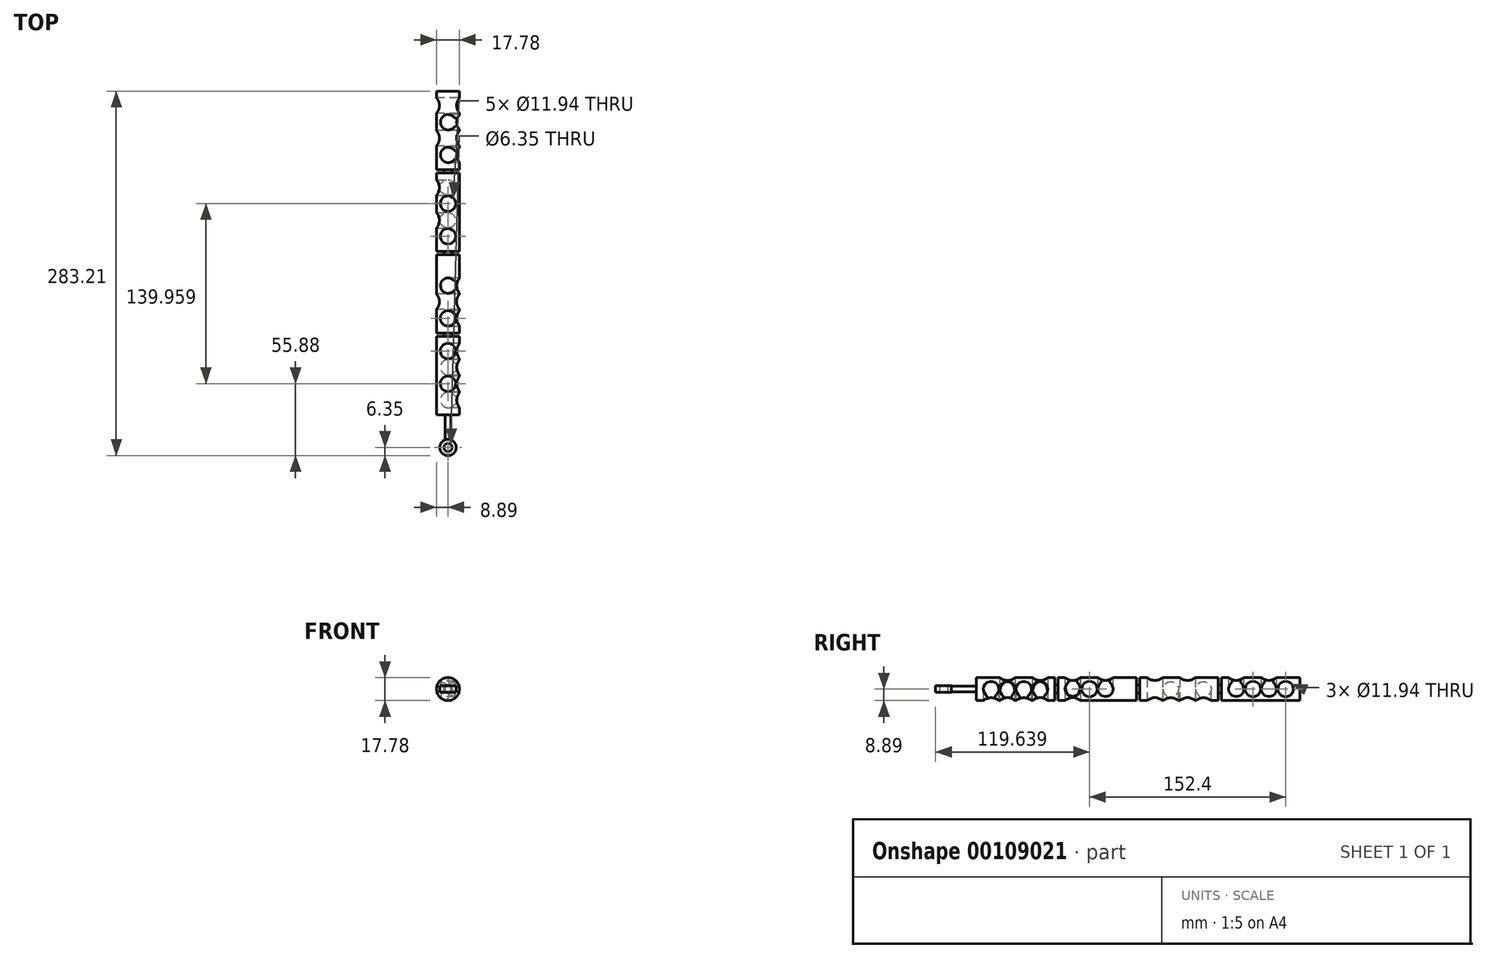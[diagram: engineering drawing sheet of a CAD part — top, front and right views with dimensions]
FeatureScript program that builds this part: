
annotation { "Feature Type Name" : "Feature", "Feature Type Description" : "" }
export const myFeature = defineFeature(function(context is Context, id is Id, definition is map)
    precondition{}
    {
        {
            var Q0;
            Q0=qCreatedBy(makeId("Front.planeOp"),FACE);
            var sketch = newSketch(context, id + "F0", { "sketchPlane" : qUnion([Q0])});
            skCircle(sketch, "E0", {"center": v(0, 0) * mm, "radius": 8.9 * mm});
            skSolve(sketch);
        }
        {
            var Q0;
            Q0=makeQuery(id+"F0.imprint","IMPRINT",FACE,{"disambiguationData":[TD([[makeQuery(id+"F0.imprint","IMPRINT",EDGE,{"derivedFrom":sQuery(id+"F0.wireOp",EDGE,"E0")}),1.0]])]});
            extrude(context, id + "F1", {"entities" : qUnion([Q0]), "oppositeDirection" : true, "depth" : 50.8 * mm});
        }
        {
            var Q0;
            Q0=qCreatedBy(makeId("Top.planeOp"),FACE);
            var sketch = newSketch(context, id + "F2", { "sketchPlane" : qUnion([Q0])});
            skCircle(sketch, "E1", {"center": v(0, 6.6) * mm, "radius": 5.97 * mm});
            skCircle(sketch, "E2", {"center": v(0, 32) * mm, "radius": 5.97 * mm});
            skLineSegment(sketch, "E3", {"start": v(0, 32) * mm, "end": v(0, 6.6) * mm});
            skLineSegment(sketch, "E4", {"start": v(0, 26.04) * mm, "end": v(0, 12.58) * mm});
            skSolve(sketch);
        }
        {
            var Q0;
            Q0=qCreatedBy(makeId("Top.planeOp"),FACE);
            cPlane(context, id + "F3", {"entities" : qUnion([Q0]), "cplaneType" : CPlaneType.OFFSET, "offset" : 25.4 * mm, "oppositeDirection" : true, "width" : 152.4 * mm, "height" : 152.4 * mm});
        }
        {
            var Q0;
            Q0=qCreatedBy(id+"F3.planeOp",FACE);
            var sketch = newSketch(context, id + "F4", { "sketchPlane" : qUnion([Q0])});
            skCircle(sketch, "E5", {"center": v(0, 19.05) * mm, "radius": 5.97 * mm});
            skLineSegment(sketch, "E6", {"start": v(0, 19.05) * mm, "end": v(0, 0) * mm});
            skLineSegment(sketch, "E7", {"start": v(0, 19.05) * mm, "end": v(0, 44.45) * mm});
            skCircle(sketch, "E8", {"center": v(0, 44.45) * mm, "radius": 5.97 * mm});
            skSolve(sketch);
        }
        {
            var Q0;
            Q0=qCreatedBy(makeId("Front.planeOp"),FACE);
            var sketch = newSketch(context, id + "F5", { "sketchPlane" : qUnion([Q0])});
            skLineSegment(sketch, "E9", {"start": v(0, -25.4) * mm, "end": v(0, -8.9) * mm});
            skArc(sketch, "E10", {"start": v(0, -8.89) * mm, "mid": v(2.6, -2.6) * mm, "end": v(8.9, 0) * mm});
            skLineSegment(sketch, "E11", {"start": v(8.9, 0) * mm, "end": v(29, 0) * mm});
            skLineSegment(sketch, "E12", {"start": v(-8.9, 0) * mm, "end": v(-22.24, 0) * mm});
            skArc(sketch, "E13", {"start": v(-8.9, 0) * mm, "mid": v(-2.6, -2.6) * mm, "end": v(0, -8.9) * mm});
            skSolve(sketch);
        }
        {
            var Q0;
            Q0=makeQuery(id+"F2.imprint","IMPRINT",FACE,{"disambiguationData":[TD([[makeQuery(id+"F2.imprint","IMPRINT",EDGE,{"derivedFrom":sQuery(id+"F2.wireOp",EDGE,"E2")}),1.0]])]});
            var Q1;
            Q1=makeQuery(id+"F2.imprint","IMPRINT",FACE,{"disambiguationData":[TD([[makeQuery(id+"F2.imprint","IMPRINT",EDGE,{"derivedFrom":sQuery(id+"F2.wireOp",EDGE,"E1")}),1.0]])]});
            extrude(context, id + "F6", {"entities" : qUnion([Q0, Q1]), "operationType" : NewBodyOperationType.REMOVE, "depth" : 25.4 * mm, "hasSecondDirection" : true, "secondDirectionOppositeDirection" : true, "secondDirectionDepth" : 25.4 * mm});
        }
        {
            var Q0;
            Q0=makeQuery(id+"F1.opExtrude","CAP_FACE",FACE,{"disambiguationData":[OSD([sQuery(id+"F0.wireOp",EDGE,"E0")])],"isStart":true});
            var sketch = newSketch(context, id + "F7", { "sketchPlane" : qUnion([Q0])});
            skCircle(sketch, "E14", {"center": v(0, 0) * mm, "radius": 3.18 * mm});
            skSolve(sketch);
        }
        {
            var Q0;
            Q0=makeQuery(id+"F7.imprint","IMPRINT",FACE,{"disambiguationData":[TD([[makeQuery(id+"F7.imprint","IMPRINT",EDGE,{"derivedFrom":sQuery(id+"F7.wireOp",EDGE,"E14")}),1.0]])]});
            extrude(context, id + "F8", {"entities" : qUnion([Q0]), "operationType" : NewBodyOperationType.ADD, "depth" : 12.7 * mm});
        }
        {
            var Q0;
            Q0=makeQuery(id+"F1.opExtrude","CAP_FACE",FACE,{"disambiguationData":[OSD([sQuery(id+"F0.wireOp",EDGE,"E0")])],"isStart":false});
            var sketch = newSketch(context, id + "F9", { "sketchPlane" : qUnion([Q0])});
            skCircle(sketch, "E15", {"center": v(0, 0) * mm, "radius": 3.18 * mm});
            skSolve(sketch);
        }
        {
            var Q0;
            Q0 = qSketchRegion(id + "F9", true);
            extrude(context, id + "F10", {"entities" : qUnion([Q0]), "operationType" : NewBodyOperationType.ADD, "depth" : 12.7 * mm});
        }
        {
            var Q0;
            Q0=makeQuery(id+"F8.opExtrude","CAP_FACE",FACE,{"disambiguationData":[OSD([sQuery(id+"F7.wireOp",EDGE,"E14")])],"isStart":false});
            var sketch = newSketch(context, id + "F11", { "sketchPlane" : qUnion([Q0])});
            skCircle(sketch, "E16", {"center": v(0, 0) * mm, "radius": 8.9 * mm});
            skSolve(sketch);
        }
        {
            var Q0;
            Q0=makeQuery(id+"F11.imprint","IMPRINT",FACE,{"disambiguationData":[TD([[makeQuery(id+"F11.imprint","IMPRINT",EDGE,{"derivedFrom":sQuery(id+"F11.wireOp",EDGE,"E16")}),1.0]])]});
            var Q1;
            Q1=makeQuery(id+"F11.imprint","IMPRINT",FACE,{"disambiguationData":[TD([[makeQuery(id+"F11.imprint","IMPRINT",EDGE,{"derivedFrom":makeQuery(id+"F8.opExtrude","CAP_EDGE",EDGE,{"disambiguationData":[OSD([sQuery(id+"F7.wireOp",EDGE,"E14")])],"isStart":false})}),1.0]])]});
            extrude(context, id + "F12", {"entities" : qUnion([Q0, Q1]), "operationType" : NewBodyOperationType.ADD, "depth" : 50.8 * mm});
        }
        {
            var Q0;
            Q0=makeQuery(id+"F10.opExtrude","CAP_FACE",FACE,{"disambiguationData":[OSD([sQuery(id+"F9.wireOp",EDGE,"E15")])],"isStart":false});
            var sketch = newSketch(context, id + "F13", { "sketchPlane" : qUnion([Q0])});
            skCircle(sketch, "E17", {"center": v(0, 0) * mm, "radius": 8.9 * mm});
            skSolve(sketch);
        }
        {
            var Q0;
            Q0=makeQuery(id+"F13.imprint","IMPRINT",FACE,{"disambiguationData":[TD([[makeQuery(id+"F13.imprint","IMPRINT",EDGE,{"derivedFrom":sQuery(id+"F13.wireOp",EDGE,"E17")}),1.0]])]});
            var Q1;
            Q1=makeQuery(id+"F13.imprint","IMPRINT",FACE,{"disambiguationData":[TD([[makeQuery(id+"F13.imprint","IMPRINT",EDGE,{"derivedFrom":makeQuery(id+"F10.opExtrude","CAP_EDGE",EDGE,{"disambiguationData":[OSD([sQuery(id+"F9.wireOp",EDGE,"E15")])],"isStart":false})}),1.0]])]});
            extrude(context, id + "F14", {"entities" : qUnion([Q0, Q1]), "operationType" : NewBodyOperationType.ADD, "depth" : 50.8 * mm});
        }
        {
            var Q0;
            Q0=makeQuery(id+"F12.opExtrude","CAP_FACE",FACE,{"disambiguationData":[OSD([sQuery(id+"F11.wireOp",EDGE,"E16")])],"isStart":false});
            var sketch = newSketch(context, id + "F15", { "sketchPlane" : qUnion([Q0])});
            skCircle(sketch, "E18", {"center": v(0, 0) * mm, "radius": 3.18 * mm});
            skSolve(sketch);
        }
        {
            var Q0;
            Q0=makeQuery(id+"F15.imprint","IMPRINT",FACE,{"disambiguationData":[TD([[makeQuery(id+"F15.imprint","IMPRINT",EDGE,{"derivedFrom":sQuery(id+"F15.wireOp",EDGE,"E18")}),1.0]])]});
            extrude(context, id + "F16", {"entities" : qUnion([Q0]), "operationType" : NewBodyOperationType.ADD, "depth" : 12.7 * mm});
        }
        {
            var Q0;
            Q0=makeQuery(id+"F16.opExtrude","CAP_FACE",FACE,{"disambiguationData":[OSD([sQuery(id+"F15.wireOp",EDGE,"E18")])],"isStart":false});
            var sketch = newSketch(context, id + "F17", { "sketchPlane" : qUnion([Q0])});
            skCircle(sketch, "E19", {"center": v(0, 0) * mm, "radius": 8.9 * mm});
            skSolve(sketch);
        }
        {
            var Q0;
            Q0=makeQuery(id+"F17.imprint","IMPRINT",FACE,{"disambiguationData":[TD([[makeQuery(id+"F17.imprint","IMPRINT",EDGE,{"derivedFrom":makeQuery(id+"F16.opExtrude","CAP_EDGE",EDGE,{"disambiguationData":[OSD([sQuery(id+"F15.wireOp",EDGE,"E18")])],"isStart":false})}),1.0]])]});
            var Q1;
            Q1=makeQuery(id+"F17.imprint","IMPRINT",FACE,{"disambiguationData":[TD([[makeQuery(id+"F17.imprint","IMPRINT",EDGE,{"derivedFrom":sQuery(id+"F17.wireOp",EDGE,"E19")}),1.0]])]});
            extrude(context, id + "F18", {"entities" : qUnion([Q0, Q1]), "operationType" : NewBodyOperationType.ADD, "depth" : 50.8 * mm});
        }
        {
            var Q0;
            Q0=qCreatedBy(makeId("Top.planeOp"),FACE);
            var sketch = newSketch(context, id + "F19", { "sketchPlane" : qUnion([Q0])});
            skLineSegment(sketch, "E20", {"start": v(0, 6.6) * mm, "end": v(0, -18.8) * mm});
            skCircle(sketch, "E21", {"center": v(0, -18.8) * mm, "radius": 5.97 * mm});
            skLineSegment(sketch, "E22", {"start": v(0, -18.8) * mm, "end": v(0, -44.2) * mm});
            skCircle(sketch, "E23", {"center": v(0, -44.2) * mm, "radius": 5.97 * mm});
            skLineSegment(sketch, "E24", {"start": v(0, -44.2) * mm, "end": v(0, -82.3) * mm});
            skCircle(sketch, "E25", {"center": v(0, -82.3) * mm, "radius": 5.97 * mm});
            skLineSegment(sketch, "E26", {"start": v(0, -82.3) * mm, "end": v(0, -107.7) * mm});
            skCircle(sketch, "E27", {"center": v(0, -107.7) * mm, "radius": 5.97 * mm});
            skLineSegment(sketch, "E28", {"start": v(0, 6.6) * mm, "end": v(0, 32) * mm});
            skLineSegment(sketch, "E29", {"start": v(0, 32) * mm, "end": v(0, 82.8) * mm});
            skCircle(sketch, "E30", {"center": v(0, 82.8) * mm, "radius": 6 * mm});
            skLineSegment(sketch, "E31", {"start": v(0, 82.8) * mm, "end": v(0, 108.2) * mm});
            skCircle(sketch, "E32", {"center": v(0, 108.2) * mm, "radius": 5.97 * mm});
            skSolve(sketch);
        }
        {
            var Q0;
            Q0=qCreatedBy(id+"F3.planeOp",FACE);
            var sketch = newSketch(context, id + "F20", { "sketchPlane" : qUnion([Q0])});
            skLineSegment(sketch, "E33", {"start": v(0, 19.05) * mm, "end": v(0, -31.75) * mm});
            skLineSegment(sketch, "E34", {"start": v(0, 44.45) * mm, "end": v(0, 69.85) * mm});
            skLineSegment(sketch, "E35", {"start": v(0, -31.75) * mm, "end": v(0, -57.15) * mm});
            skLineSegment(sketch, "E36", {"start": v(0, -57.15) * mm, "end": v(0, -82.55) * mm});
            skLineSegment(sketch, "E37", {"start": v(0, -82.55) * mm, "end": v(0, -107.95) * mm});
            skLineSegment(sketch, "E38", {"start": v(0, 69.85) * mm, "end": v(0, 95.25) * mm});
            skCircle(sketch, "E39", {"center": v(0, 69.85) * mm, "radius": 5.97 * mm});
            skCircle(sketch, "E40", {"center": v(0, 95.25) * mm, "radius": 5.97 * mm});
            skCircle(sketch, "E41", {"center": v(0, -31.75) * mm, "radius": 5.97 * mm});
            skCircle(sketch, "E42", {"center": v(0, -57.15) * mm, "radius": 5.97 * mm});
            skCircle(sketch, "E43", {"center": v(0, -82.55) * mm, "radius": 5.97 * mm});
            skCircle(sketch, "E44", {"center": v(0, -107.95) * mm, "radius": 5.97 * mm});
            skLineSegment(sketch, "E45", {"start": v(0, -82.55) * mm, "end": v(0, -95.25) * mm});
            skCircle(sketch, "E46", {"center": v(0, -95.25) * mm, "radius": 5.97 * mm});
            skLineSegment(sketch, "E47", {"start": v(0, -107.95) * mm, "end": v(0, -120.65) * mm});
            skCircle(sketch, "E48", {"center": v(0, -120.65) * mm, "radius": 5.97 * mm});
            skLineSegment(sketch, "E49", {"start": v(0, -120.65) * mm, "end": v(0, -127) * mm});
            skSolve(sketch);
        }
        {
            var Q0;
            Q0=qCreatedBy(makeId("Top.planeOp"),FACE);
            cPlane(context, id + "F21", {"entities" : qUnion([Q0]), "cplaneType" : CPlaneType.OFFSET, "offset" : 25.4 * mm, "width" : 152.4 * mm, "height" : 152.4 * mm});
        }
        {
            var Q0;
            Q0=qCreatedBy(makeId("Right.planeOp"),FACE);
            var sketch = newSketch(context, id + "F22", { "sketchPlane" : qUnion([Q0])});
            skLineSegment(sketch, "E50", {"start": v(108.2, 0) * mm, "end": v(82.8, 0) * mm});
            skLineSegment(sketch, "E51", {"start": v(-18.8, 0) * mm, "end": v(-44.2, 0) * mm});
            skLineSegment(sketch, "E52", {"start": v(-44.2, 0) * mm, "end": v(-82.3, 0) * mm});
            skLineSegment(sketch, "E53", {"start": v(-82.3, 0) * mm, "end": v(-107.7, 0) * mm});
            skCircle(sketch, "E54", {"center": v(108.2, 0) * mm, "radius": 5.97 * mm});
            skCircle(sketch, "E55", {"center": v(82.8, 0) * mm, "radius": 5.97 * mm});
            skCircle(sketch, "E56", {"center": v(-18.8, 0) * mm, "radius": 5.97 * mm});
            skCircle(sketch, "E57", {"center": v(-44.2, 0) * mm, "radius": 5.97 * mm});
            skCircle(sketch, "E58", {"center": v(-82.3, 0) * mm, "radius": 5.97 * mm});
            skCircle(sketch, "E59", {"center": v(-107.7, 0) * mm, "radius": 5.97 * mm});
            skLineSegment(sketch, "E60", {"start": v(-44.2, 0) * mm, "end": v(-95, 0) * mm});
            skLineSegment(sketch, "E61", {"start": v(-18.8, 0) * mm, "end": v(82.8, 0) * mm});
            skSolve(sketch);
        }
        {
            var Q0;
            Q0=makeQuery(id+"F22.imprint","IMPRINT",FACE,{"disambiguationData":[TD([[makeQuery(id+"F22.imprint","IMPRINT",EDGE,{"derivedFrom":sQuery(id+"F22.wireOp",EDGE,"E54")}),1.0]])]});
            var Q1;
            {var subQ0=sQuery(id+"F22.wireOp",EDGE,"64IQ4rFp-FNV7-kNIL-IrGJ-L7VyzQQre0IC");var subQ1=sQuery(id+"F22.wireOp",EDGE,"E50");var subQ2=makeQuery(id+"F22.imprint","INTERSECT",VERTEX,{"derivedFrom":[subQ1,subQ0]});Q1=makeQuery(id+"F22.imprint","IMPRINT",FACE,{"disambiguationData":[TD([[makeQuery(id+"F22.imprint","IMPRINT",EDGE,{"disambiguationData":[TD([[subQ2,1.0]])],"derivedFrom":subQ1}),-1.0]])]});}
            var Q2;
            {var subQ0=sQuery(id+"F22.wireOp",EDGE,"64IQ4rFp-FNV7-kNIL-IrGJ-L7VyzQQre0IC");var subQ1=sQuery(id+"F22.wireOp",EDGE,"E50");var subQ2=makeQuery(id+"F22.imprint","INTERSECT",VERTEX,{"derivedFrom":[subQ1,subQ0]});Q2=makeQuery(id+"F22.imprint","IMPRINT",FACE,{"disambiguationData":[TD([[makeQuery(id+"F22.imprint","IMPRINT",EDGE,{"disambiguationData":[TD([[subQ2,1.0]])],"derivedFrom":subQ1}),1.0]])]});}
            var Q3;
            {var subQ0=sQuery(id+"F22.wireOp",EDGE,"E51");var subQ1=sQuery(id+"F22.wireOp",EDGE,"64IQ4rFp-FNV7-kNIL-IrGJ-L7VyzQQre0IC");var subQ2=makeQuery(id+"F22.imprint","INTERSECT",VERTEX,{"derivedFrom":[subQ1,subQ0]});Q3=makeQuery(id+"F22.imprint","IMPRINT",FACE,{"disambiguationData":[TD([[makeQuery(id+"F22.imprint","IMPRINT",EDGE,{"disambiguationData":[TD([[subQ2,1.0]])],"derivedFrom":subQ1}),1.0]])]});}
            var Q4;
            {var subQ0=sQuery(id+"F22.wireOp",EDGE,"E51");var subQ1=sQuery(id+"F22.wireOp",EDGE,"64IQ4rFp-FNV7-kNIL-IrGJ-L7VyzQQre0IC");var subQ2=makeQuery(id+"F22.imprint","INTERSECT",VERTEX,{"derivedFrom":[subQ1,subQ0]});Q4=makeQuery(id+"F22.imprint","IMPRINT",FACE,{"disambiguationData":[TD([[makeQuery(id+"F22.imprint","IMPRINT",EDGE,{"disambiguationData":[TD([[subQ2,1.0]])],"derivedFrom":subQ1}),-1.0]])]});}
            var Q5;
            {var subQ0=sQuery(id+"F22.wireOp",EDGE,"E52");var subQ1=sQuery(id+"F22.wireOp",EDGE,"E51");var subQ2=makeQuery(id+"F22.imprint","INTERSECT",VERTEX,{"derivedFrom":[subQ1,subQ0]});Q5=makeQuery(id+"F22.imprint","IMPRINT",FACE,{"disambiguationData":[TD([[makeQuery(id+"F22.imprint","IMPRINT",EDGE,{"disambiguationData":[TD([[subQ2,1.0]])],"derivedFrom":subQ1}),-1.0]])]});}
            var Q6;
            {var subQ0=sQuery(id+"F22.wireOp",EDGE,"E52");var subQ1=sQuery(id+"F22.wireOp",EDGE,"E51");var subQ2=makeQuery(id+"F22.imprint","INTERSECT",VERTEX,{"derivedFrom":[subQ1,subQ0]});Q6=makeQuery(id+"F22.imprint","IMPRINT",FACE,{"disambiguationData":[TD([[makeQuery(id+"F22.imprint","IMPRINT",EDGE,{"disambiguationData":[TD([[subQ2,1.0]])],"derivedFrom":subQ1}),1.0]])]});}
            var Q7;
            Q7=sQuery(id+"F22.wireOp",EDGE,"E54");
            extrude(context, id + "F23", {"entities" : qUnion([Q0, Q1, Q2, Q3, Q4, Q5, Q6]), "operationType" : NewBodyOperationType.REMOVE, "surfaceEntities" : qUnion([Q7]), "depth" : 25.4 * mm, "hasSecondDirection" : true, "secondDirectionOppositeDirection" : true, "secondDirectionDepth" : 25.4 * mm});
        }
        {
            var Q0;
            Q0=qCreatedBy(id+"F21.planeOp",FACE);
            var sketch = newSketch(context, id + "F24", { "sketchPlane" : qUnion([Q0])});
            skLineSegment(sketch, "E62", {"start": v(0, 69.85) * mm, "end": v(0, 116.23) * mm});
            skCircle(sketch, "E63", {"center": v(0, 69.85) * mm, "radius": 5.97 * mm});
            skCircle(sketch, "E64", {"center": v(0, 95.25) * mm, "radius": 5.97 * mm});
            skCircle(sketch, "E65", {"center": v(0, -31.75) * mm, "radius": 5.97 * mm});
            skCircle(sketch, "E66", {"center": v(0, -57.15) * mm, "radius": 5.97 * mm});
            skCircle(sketch, "E67", {"center": v(0, -82.55) * mm, "radius": 5.97 * mm});
            skCircle(sketch, "E68", {"center": v(0, -107.95) * mm, "radius": 5.97 * mm});
            skSolve(sketch);
        }
        {
            var Q0;
            Q0=qCreatedBy(makeId("Front.planeOp"),FACE);
            var sketch = newSketch(context, id + "F25", { "sketchPlane" : qUnion([Q0])});
            skLineSegment(sketch, "E69", {"start": v(13.2, 0) * mm, "end": v(8.9, 0) * mm});
            skLineSegment(sketch, "E70", {"start": v(0, 25.4) * mm, "end": v(0, 8.9) * mm});
            skLineSegment(sketch, "E71", {"start": v(8.9, 0) * mm, "end": v(13.2, 0) * mm});
            skArc(sketch, "E72", {"start": v(0, 8.89) * mm, "mid": v(2.6, 2.6) * mm, "end": v(8.9, 0) * mm});
            skSolve(sketch);
        }
        {
            var Q0;
            Q0=makeQuery(id+"F4.imprint","IMPRINT",FACE,{"disambiguationData":[TD([[makeQuery(id+"F4.imprint","IMPRINT",EDGE,{"derivedFrom":sQuery(id+"F4.wireOp",EDGE,"E8")}),1.0]])]});
            var Q1;
            {var subQ0=sQuery(id+"F4.wireOp",EDGE,"E6");var subQ1=sQuery(id+"F4.wireOp",EDGE,"E5");var subQ2=makeQuery(id+"F4.imprint","INTERSECT",VERTEX,{"derivedFrom":[subQ1,subQ0]});Q1=makeQuery(id+"F4.imprint","IMPRINT",FACE,{"disambiguationData":[TD([[makeQuery(id+"F4.imprint","IMPRINT",EDGE,{"disambiguationData":[TD([[subQ2,-1.0]])],"derivedFrom":subQ1}),1.0]])]});}
            var Q2;
            {var subQ0=sQuery(id+"F4.wireOp",EDGE,"E6");var subQ1=sQuery(id+"F4.wireOp",EDGE,"E5");var subQ2=makeQuery(id+"F4.imprint","INTERSECT",VERTEX,{"derivedFrom":[subQ1,subQ0]});Q2=makeQuery(id+"F4.imprint","IMPRINT",FACE,{"disambiguationData":[TD([[makeQuery(id+"F4.imprint","IMPRINT",EDGE,{"disambiguationData":[TD([[subQ2,1.0]])],"derivedFrom":subQ1}),1.0]])]});}
            var Q3;
            Q3=sQuery(id+"F5.wireOp",EDGE,"E9");
            var Q4;
            Q4=sQuery(id+"F5.wireOp",EDGE,"E13");
            var Q5;
            Q5=sQuery(id+"F5.wireOp",EDGE,"E12");
            sweep(context, id + "F26", {"operationType" : NewBodyOperationType.REMOVE, "profiles" : qUnion([Q0, Q1, Q2]), "path" : qUnion([Q3, Q4, Q5])});
        }
        {
            var Q0;
            Q0=makeQuery(id+"F24.imprint","IMPRINT",FACE,{"disambiguationData":[TD([[makeQuery(id+"F24.imprint","IMPRINT",EDGE,{"derivedFrom":sQuery(id+"F24.wireOp",EDGE,"E66")}),1.0]])]});
            var Q1;
            Q1=makeQuery(id+"F24.imprint","IMPRINT",FACE,{"disambiguationData":[TD([[makeQuery(id+"F24.imprint","IMPRINT",EDGE,{"derivedFrom":sQuery(id+"F24.wireOp",EDGE,"E65")}),1.0]])]});
            var Q2;
            Q2=makeQuery(id+"F24.imprint","IMPRINT",FACE,{"disambiguationData":[TD([[makeQuery(id+"F24.imprint","IMPRINT",EDGE,{"derivedFrom":sQuery(id+"F24.wireOp",EDGE,"E63")}),1.0]])]});
            var Q3;
            Q3=makeQuery(id+"F24.imprint","IMPRINT",FACE,{"disambiguationData":[TD([[makeQuery(id+"F24.imprint","IMPRINT",EDGE,{"derivedFrom":sQuery(id+"F24.wireOp",EDGE,"E64")}),1.0]])]});
            var Q4;
            Q4=sQuery(id+"F25.wireOp",EDGE,"E70");
            var Q5;
            Q5=sQuery(id+"F25.wireOp",EDGE,"E72");
            var Q6;
            Q6=sQuery(id+"F5.wireOp",EDGE,"E11");
            sweep(context, id + "F27", {"operationType" : NewBodyOperationType.REMOVE, "profiles" : qUnion([Q0, Q1, Q2, Q3]), "path" : qUnion([Q4, Q5, Q6])});
        }
        {
            var Q0;
            {var subQ0=sQuery(id+"F20.wireOp",EDGE,"E47");var subQ1=sQuery(id+"F20.wireOp",EDGE,"E37");var subQ2=makeQuery(id+"F20.imprint","INTERSECT",VERTEX,{"derivedFrom":[subQ1,subQ0]});Q0=makeQuery(id+"F20.imprint","IMPRINT",FACE,{"disambiguationData":[TD([[makeQuery(id+"F20.imprint","IMPRINT",EDGE,{"disambiguationData":[TD([[subQ2,1.0]])],"derivedFrom":subQ1}),1.0]])]});}
            var Q1;
            {var subQ0=sQuery(id+"F20.wireOp",EDGE,"E47");var subQ1=sQuery(id+"F20.wireOp",EDGE,"E37");var subQ2=makeQuery(id+"F20.imprint","INTERSECT",VERTEX,{"derivedFrom":[subQ1,subQ0]});Q1=makeQuery(id+"F20.imprint","IMPRINT",FACE,{"disambiguationData":[TD([[makeQuery(id+"F20.imprint","IMPRINT",EDGE,{"disambiguationData":[TD([[subQ2,1.0]])],"derivedFrom":subQ1}),-1.0]])]});}
            var Q2;
            {var subQ0=sQuery(id+"F20.wireOp",EDGE,"E45");var subQ1=sQuery(id+"F20.wireOp",EDGE,"E36");var subQ2=makeQuery(id+"F20.imprint","INTERSECT",VERTEX,{"derivedFrom":[subQ1,subQ0]});Q2=makeQuery(id+"F20.imprint","IMPRINT",FACE,{"disambiguationData":[TD([[makeQuery(id+"F20.imprint","IMPRINT",EDGE,{"disambiguationData":[TD([[subQ2,1.0]])],"derivedFrom":subQ1}),1.0]])]});}
            var Q3;
            {var subQ0=sQuery(id+"F20.wireOp",EDGE,"E45");var subQ1=sQuery(id+"F20.wireOp",EDGE,"E36");var subQ2=makeQuery(id+"F20.imprint","INTERSECT",VERTEX,{"derivedFrom":[subQ1,subQ0]});Q3=makeQuery(id+"F20.imprint","IMPRINT",FACE,{"disambiguationData":[TD([[makeQuery(id+"F20.imprint","IMPRINT",EDGE,{"disambiguationData":[TD([[subQ2,1.0]])],"derivedFrom":subQ1}),-1.0]])]});}
            extrude(context, id + "F28", {"entities" : qUnion([Q0, Q1, Q2, Q3]), "operationType" : NewBodyOperationType.REMOVE, "depth" : 50.8 * mm});
        }
        {
            var Q0;
            Q0=makeQuery(id+"F20.imprint","IMPRINT",FACE,{"disambiguationData":[TD([[makeQuery(id+"F20.imprint","IMPRINT",EDGE,{"derivedFrom":sQuery(id+"F20.wireOp",EDGE,"E48")}),1.0]])]});
            var Q1;
            {var subQ0=sQuery(id+"F20.wireOp",EDGE,"E45");var subQ1=sQuery(id+"F20.wireOp",EDGE,"E37");var subQ2=makeQuery(id+"F20.imprint","INTERSECT",VERTEX,{"derivedFrom":[subQ1,subQ0]});Q1=makeQuery(id+"F20.imprint","IMPRINT",FACE,{"disambiguationData":[TD([[makeQuery(id+"F20.imprint","IMPRINT",EDGE,{"disambiguationData":[TD([[subQ2,-1.0]])],"derivedFrom":subQ1}),1.0]])]});}
            var Q2;
            {var subQ0=sQuery(id+"F20.wireOp",EDGE,"E45");var subQ1=sQuery(id+"F20.wireOp",EDGE,"E37");var subQ2=makeQuery(id+"F20.imprint","INTERSECT",VERTEX,{"derivedFrom":[subQ1,subQ0]});Q2=makeQuery(id+"F20.imprint","IMPRINT",FACE,{"disambiguationData":[TD([[makeQuery(id+"F20.imprint","IMPRINT",EDGE,{"disambiguationData":[TD([[subQ2,-1.0]])],"derivedFrom":subQ1}),-1.0]])]});}
            var Q3;
            Q3=sQuery(id+"F5.wireOp",EDGE,"E9");
            var Q4;
            Q4=sQuery(id+"F5.wireOp",EDGE,"E10");
            var Q5;
            Q5=sQuery(id+"F5.wireOp",EDGE,"E11");
            sweep(context, id + "F29", {"operationType" : NewBodyOperationType.REMOVE, "profiles" : qUnion([Q0, Q1, Q2]), "path" : qUnion([Q3, Q4, Q5])});
        }
        {
            var Q0;
            Q0=makeQuery(id+"F18.opExtrude","CAP_FACE",FACE,{"disambiguationData":[OSD([sQuery(id+"F17.wireOp",EDGE,"E19")])],"isStart":false});
            extrude(context, id + "F30", {"entities" : qUnion([Q0]), "operationType" : NewBodyOperationType.ADD, "depth" : 5.08 * mm});
        }
        {
            var Q0;
            Q0=makeQuery(id+"F18.opExtrude","CAP_FACE",FACE,{"disambiguationData":[OSD([sQuery(id+"F17.wireOp",EDGE,"E19")])],"isStart":true});
            extrude(context, id + "F31", {"entities" : qUnion([Q0]), "operationType" : NewBodyOperationType.ADD, "depth" : 5.08 * mm});
        }
        {
            var Q0;
            Q0=makeQuery(id+"F12.opExtrude","CAP_FACE",FACE,{"disambiguationData":[OSD([sQuery(id+"F11.wireOp",EDGE,"E16")])],"isStart":false});
            extrude(context, id + "F32", {"entities" : qUnion([Q0]), "operationType" : NewBodyOperationType.ADD, "depth" : 5.08 * mm});
        }
        {
            var Q0;
            Q0=makeQuery(id+"F1.opExtrude","CAP_FACE",FACE,{"disambiguationData":[OSD([sQuery(id+"F0.wireOp",EDGE,"E0")])],"isStart":true});
            extrude(context, id + "F33", {"entities" : qUnion([Q0]), "operationType" : NewBodyOperationType.ADD, "depth" : 5.08 * mm});
        }
        {
            var Q0;
            Q0=makeQuery(id+"F12.opExtrude","CAP_FACE",FACE,{"disambiguationData":[OSD([sQuery(id+"F11.wireOp",EDGE,"E16")])],"isStart":true});
            extrude(context, id + "F34", {"entities" : qUnion([Q0]), "operationType" : NewBodyOperationType.ADD, "depth" : 5.08 * mm});
        }
        {
            var Q0;
            Q0=makeQuery(id+"F1.opExtrude","CAP_FACE",FACE,{"disambiguationData":[OSD([sQuery(id+"F0.wireOp",EDGE,"E0")])],"isStart":false});
            extrude(context, id + "F35", {"entities" : qUnion([Q0]), "operationType" : NewBodyOperationType.ADD, "depth" : 5.08 * mm});
        }
        {
            var Q0;
            Q0=makeQuery(id+"F14.opExtrude","CAP_FACE",FACE,{"disambiguationData":[OSD([sQuery(id+"F13.wireOp",EDGE,"E17")])],"isStart":true});
            extrude(context, id + "F36", {"entities" : qUnion([Q0]), "operationType" : NewBodyOperationType.ADD, "depth" : 5.08 * mm});
        }
        {
            var Q0;
            Q0=makeQuery(id+"F14.opExtrude","CAP_FACE",FACE,{"disambiguationData":[OSD([sQuery(id+"F13.wireOp",EDGE,"E17")])],"isStart":false});
            extrude(context, id + "F37", {"entities" : qUnion([Q0]), "operationType" : NewBodyOperationType.ADD, "depth" : 5.08 * mm});
        }
        {
            var Q0;
            Q0=makeQuery(id+"F30.opExtrude","CAP_FACE",FACE,{"disambiguationData":[OSD([sQuery(id+"F17.wireOp",EDGE,"E19")])],"isStart":false});
            var sketch = newSketch(context, id + "F38", { "sketchPlane" : qUnion([Q0])});
            skCircle(sketch, "E73", {"center": v(0, 0) * mm, "radius": 2.29 * mm});
            skSolve(sketch);
        }
        {
            var Q0;
            Q0=qCreatedBy(makeId("Right.planeOp"),FACE);
            var sketch = newSketch(context, id + "F39", { "sketchPlane" : qUnion([Q0])});
            skLineSegment(sketch, "E74", {"start": v(-132.08, 0) * mm, "end": v(-157.48, 0) * mm});
            skCircle(sketch, "E75", {"center": v(-157.48, 0) * mm, "radius": 3.81 * mm});
            skSolve(sketch);
        }
        {
            var Q0;
            Q0=makeQuery(id+"F38.imprint","IMPRINT",FACE,{"disambiguationData":[TD([[makeQuery(id+"F38.imprint","IMPRINT",EDGE,{"derivedFrom":sQuery(id+"F38.wireOp",EDGE,"E73")}),1.0]])]});
            var Q1;
            Q1=sQuery(id+"F39.wireOp",EDGE,"E74");
            sweep(context, id + "F40", {"operationType" : NewBodyOperationType.ADD, "profiles" : qUnion([Q0]), "path" : qUnion([Q1])});
        }
        {
            var Q0;
            Q0=qCreatedBy(makeId("Top.planeOp"),FACE);
            var sketch = newSketch(context, id + "F41", { "sketchPlane" : qUnion([Q0])});
            skCircle(sketch, "E76", {"center": v(0, -157.48) * mm, "radius": 3.18 * mm});
            skCircle(sketch, "E77", {"center": v(0, -157.48) * mm, "radius": 6.35 * mm});
            skSolve(sketch);
        }
        {
            var Q0;
            Q0=makeQuery(id+"F41.imprint","IMPRINT",FACE,{"disambiguationData":[TD([[makeQuery(id+"F41.imprint","IMPRINT",EDGE,{"derivedFrom":sQuery(id+"F41.wireOp",EDGE,"E76")}),1.0]])]});
            extrude(context, id + "F42", {"entities" : qUnion([Q0]), "operationType" : NewBodyOperationType.REMOVE, "depth" : 12.7 * mm, "hasSecondDirection" : true, "secondDirectionOppositeDirection" : true, "secondDirectionDepth" : 12.7 * mm});
        }
        {
            var Q0;
            Q0=makeQuery(id+"F41.imprint","IMPRINT",FACE,{"disambiguationData":[TD([[makeQuery(id+"F41.imprint","IMPRINT",EDGE,{"derivedFrom":sQuery(id+"F41.wireOp",EDGE,"E76")}),-1.0]])]});
            extrude(context, id + "F43", {"entities" : qUnion([Q0]), "operationType" : NewBodyOperationType.ADD, "depth" : 2.54 * mm, "hasSecondDirection" : true, "secondDirectionOppositeDirection" : true, "secondDirectionDepth" : 2.54 * mm});
        }
    });
